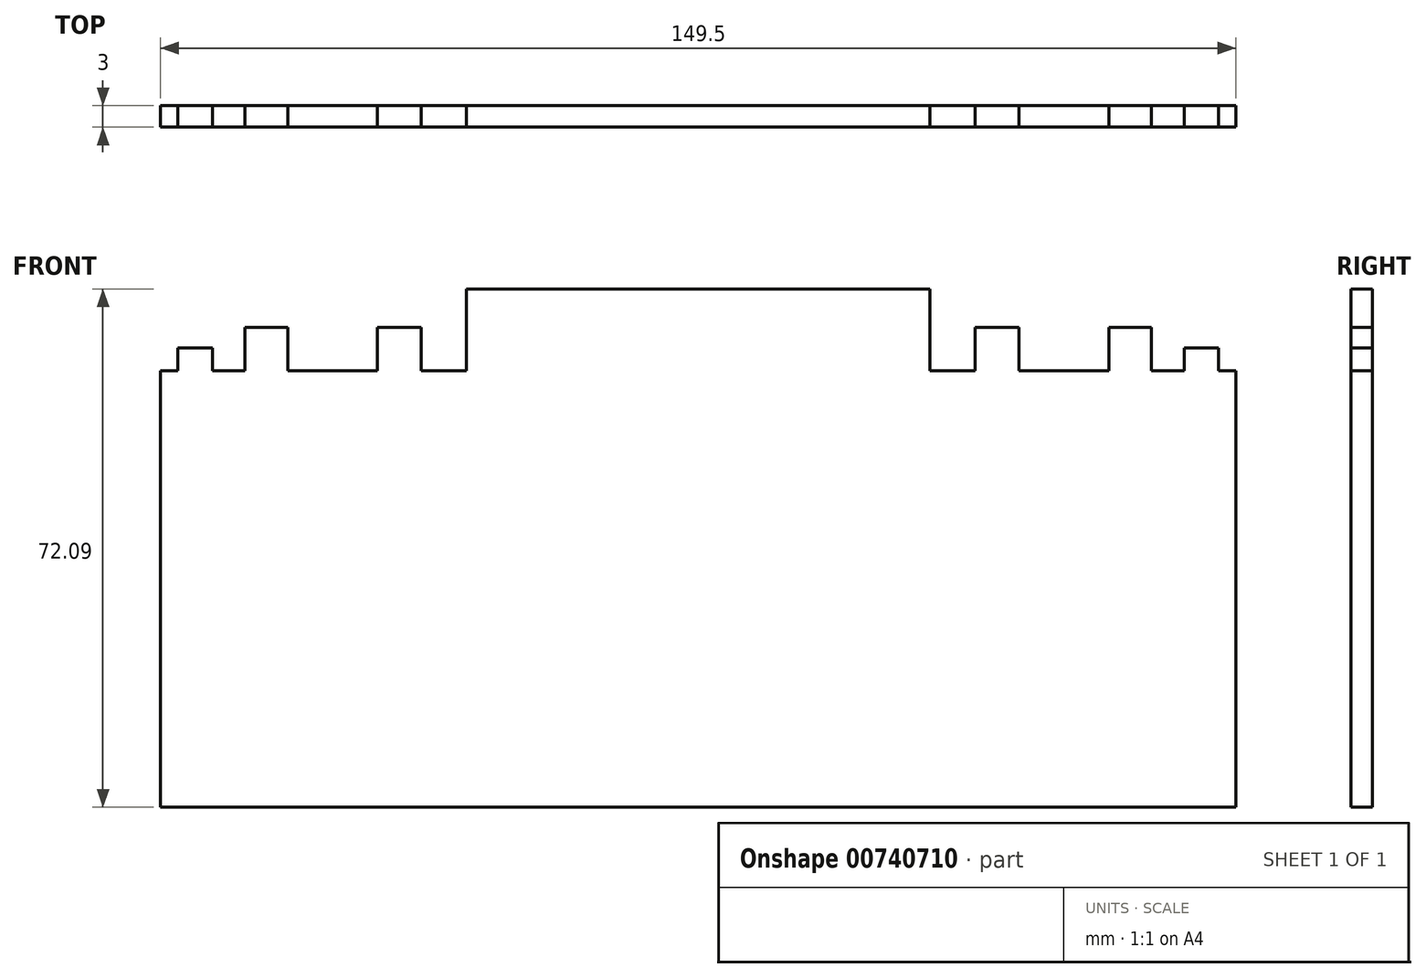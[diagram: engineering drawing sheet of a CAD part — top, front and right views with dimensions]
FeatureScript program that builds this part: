
annotation { "Feature Type Name" : "Feature", "Feature Type Description" : "" }
export const myFeature = defineFeature(function(context is Context, id is Id, definition is map)
    precondition{}
    {
        {
            var Q0;
            Q0=qCreatedBy(makeId("Front.planeOp"),FACE);
            var sketch = newSketch(context, id + "F0", { "sketchPlane" : qUnion([Q0])});
            skLineSegment(sketch, "E0", {"start": v(-74.75, 58.33) * mm, "end": v(-74.75, 0) * mm});
            skLineSegment(sketch, "E1", {"start": v(-74.75, 0) * mm, "end": v(74.54, 0) * mm});
            skLineSegment(sketch, "E2", {"start": v(-74.75, 58.33) * mm, "end": v(-74.75, 60.7) * mm});
            skLineSegment(sketch, "E3", {"start": v(-74.75, 60.7) * mm, "end": v(-38.54, 60.7) * mm});
            skLineSegment(sketch, "E4", {"start": v(-38.54, 60.7) * mm, "end": v(-38.54, 60.7) * mm});
            skLineSegment(sketch, "E5", {"start": v(-38.54, 60.7) * mm, "end": v(0, 60.7) * mm});
            skLineSegment(sketch, "E6", {"start": v(0, 60.7) * mm, "end": v(-38.54, 60.7) * mm});
            skLineSegment(sketch, "E7", {"start": v(0, 60.7) * mm, "end": v(0, 60.7) * mm});
            skLineSegment(sketch, "E8", {"start": v(-38.54, 60.7) * mm, "end": v(-38.54, 58.33) * mm});
            skLineSegment(sketch, "E9", {"start": v(-38.54, 58.33) * mm, "end": v(0, 58.33) * mm});
            skLineSegment(sketch, "E10", {"start": v(-38.54, 58.33) * mm, "end": v(-41.46, 58.33) * mm});
            skLineSegment(sketch, "E11", {"start": v(-41.46, 58.33) * mm, "end": v(-41.46, 0) * mm});
            skLineSegment(sketch, "E12", {"start": v(-41.46, 0) * mm, "end": v(-34.39, 0) * mm});
            skLineSegment(sketch, "E13", {"start": v(-34.39, 0) * mm, "end": v(-34.39, 58.33) * mm});
            skLineSegment(sketch, "E14", {"start": v(-20.6, 58.33) * mm, "end": v(-20.6, 0) * mm});
            skLineSegment(sketch, "E15", {"start": v(-20.6, 0) * mm, "end": v(-13.52, 0) * mm});
            skLineSegment(sketch, "E16", {"start": v(-13.52, 0) * mm, "end": v(-13.52, 58.33) * mm});
            skLineSegment(sketch, "E17", {"start": v(-13.52, 58.33) * mm, "end": v(-20.6, 58.33) * mm});
            skLineSegment(sketch, "E18", {"start": v(-41.46, 58.33) * mm, "end": v(-38.54, 58.33) * mm});
            skLineSegment(sketch, "E19", {"start": v(-44.62, 60.7) * mm, "end": v(-44.62, 66.71) * mm});
            skLineSegment(sketch, "E20", {"start": v(-44.62, 66.71) * mm, "end": v(-38.54, 66.71) * mm});
            skLineSegment(sketch, "E21", {"start": v(-44.62, 60.7) * mm, "end": v(-38.54, 60.7) * mm});
            skLineSegment(sketch, "E22", {"start": v(-57.08, 66.71) * mm, "end": v(-57.08, 60.7) * mm});
            skLineSegment(sketch, "E23", {"start": v(-57.08, 60.7) * mm, "end": v(-63.03, 60.7) * mm});
            skLineSegment(sketch, "E24", {"start": v(-63.03, 60.7) * mm, "end": v(-63.03, 66.71) * mm});
            skLineSegment(sketch, "E25", {"start": v(-63.03, 66.71) * mm, "end": v(-57.08, 66.71) * mm});
            skLineSegment(sketch, "E26", {"start": v(-72.38, 60.7) * mm, "end": v(-72.38, 63.88) * mm});
            skLineSegment(sketch, "E27", {"start": v(-72.38, 63.88) * mm, "end": v(-67.56, 63.88) * mm});
            skLineSegment(sketch, "E28", {"start": v(-67.56, 63.88) * mm, "end": v(-67.56, 60.7) * mm});
            skLineSegment(sketch, "E29.MirrorCS", {"start": v(74.75, 58.33) * mm, "end": v(74.75, 0) * mm});
            skLineSegment(sketch, "E30.MirrorCS", {"start": v(74.75, 0) * mm, "end": v(-74.54, 0) * mm});
            skLineSegment(sketch, "E31.MirrorCS", {"start": v(38.54, 60.7) * mm, "end": v(38.54, 58.33) * mm});
            skLineSegment(sketch, "E32.MirrorCS", {"start": v(41.46, 58.33) * mm, "end": v(38.54, 58.33) * mm});
            skLineSegment(sketch, "E33.MirrorCS", {"start": v(44.62, 60.7) * mm, "end": v(38.54, 60.7) * mm});
            skLineSegment(sketch, "E34.MirrorCS", {"start": v(38.54, 58.33) * mm, "end": v(41.46, 58.33) * mm});
            skLineSegment(sketch, "E35.MirrorCS", {"start": v(72.38, 63.88) * mm, "end": v(67.56, 63.88) * mm});
            skLineSegment(sketch, "E36.MirrorCS", {"start": v(57.08, 66.71) * mm, "end": v(57.08, 60.7) * mm});
            skLineSegment(sketch, "E37.MirrorCS", {"start": v(57.08, 60.7) * mm, "end": v(63.03, 60.7) * mm});
            skLineSegment(sketch, "E38.MirrorCS", {"start": v(63.03, 60.7) * mm, "end": v(63.03, 66.71) * mm});
            skLineSegment(sketch, "E39.MirrorCS", {"start": v(72.38, 60.7) * mm, "end": v(72.38, 63.88) * mm});
            skLineSegment(sketch, "E40.MirrorCS", {"start": v(44.62, 60.7) * mm, "end": v(44.62, 66.71) * mm});
            skLineSegment(sketch, "E41.MirrorCS", {"start": v(67.56, 63.88) * mm, "end": v(67.56, 60.7) * mm});
            skLineSegment(sketch, "E42.MirrorCS", {"start": v(74.75, 58.33) * mm, "end": v(74.75, 60.7) * mm});
            skLineSegment(sketch, "E43.MirrorCS", {"start": v(63.03, 66.71) * mm, "end": v(57.08, 66.71) * mm});
            skLineSegment(sketch, "E44.MirrorCS", {"start": v(13.52, 58.33) * mm, "end": v(20.6, 58.33) * mm});
            skLineSegment(sketch, "E45.MirrorCS", {"start": v(38.54, 60.7) * mm, "end": v(38.54, 60.7) * mm});
            skLineSegment(sketch, "E46.MirrorCS", {"start": v(44.62, 66.71) * mm, "end": v(38.54, 66.71) * mm});
            skLineSegment(sketch, "E47.MirrorCS", {"start": v(38.54, 58.33) * mm, "end": v(0, 58.33) * mm});
            skLineSegment(sketch, "E48.MirrorCS", {"start": v(20.6, 0) * mm, "end": v(13.52, 0) * mm});
            skLineSegment(sketch, "E49.MirrorCS", {"start": v(13.52, 0) * mm, "end": v(13.52, 58.33) * mm});
            skLineSegment(sketch, "E50.MirrorCS", {"start": v(34.39, 0) * mm, "end": v(34.39, 58.33) * mm});
            skLineSegment(sketch, "E51.MirrorCS", {"start": v(74.75, 60.7) * mm, "end": v(38.54, 60.7) * mm});
            skLineSegment(sketch, "E52.MirrorCS", {"start": v(20.6, 58.33) * mm, "end": v(20.6, 0) * mm});
            skLineSegment(sketch, "E53.MirrorCS", {"start": v(38.54, 60.7) * mm, "end": v(0, 60.7) * mm});
            skLineSegment(sketch, "E54.MirrorCS", {"start": v(41.46, 0) * mm, "end": v(34.39, 0) * mm});
            skLineSegment(sketch, "E55.MirrorCS", {"start": v(0, 60.7) * mm, "end": v(38.54, 60.7) * mm});
            skLineSegment(sketch, "E56.MirrorCS", {"start": v(41.46, 58.33) * mm, "end": v(41.46, 0) * mm});
            skLineSegment(sketch, "E57", {"start": v(38.54, 66.71) * mm, "end": v(38.54, 60.7) * mm});
            skLineSegment(sketch, "E58", {"start": v(-38.54, 60.7) * mm, "end": v(-38.54, 66.71) * mm});
            skLineSegment(sketch, "E59", {"start": v(-32.21, 60.7) * mm, "end": v(-32.21, 72.1) * mm});
            skLineSegment(sketch, "E60", {"start": v(-32.21, 72.1) * mm, "end": v(0, 72.1) * mm});
            skLineSegment(sketch, "E61", {"start": v(0, 72.1) * mm, "end": v(-32.21, 60.7) * mm});
            skLineSegment(sketch, "E62.MirrorCS", {"start": v(32.21, 72.1) * mm, "end": v(0, 72.1) * mm});
            skLineSegment(sketch, "E63.MirrorCS", {"start": v(32.21, 60.7) * mm, "end": v(32.21, 72.1) * mm});
            skLineSegment(sketch, "E64.MirrorCS", {"start": v(0, 72.1) * mm, "end": v(32.21, 60.7) * mm});
            skSolve(sketch);
        }
        {
            var Q0;
            Q0 = qSketchRegion(id + "F0", true);
            extrude(context, id + "F1", {"entities" : qUnion([Q0]), "depth" : 3 * mm, "offsetDistance" : 25 * mm});
        }
    });
